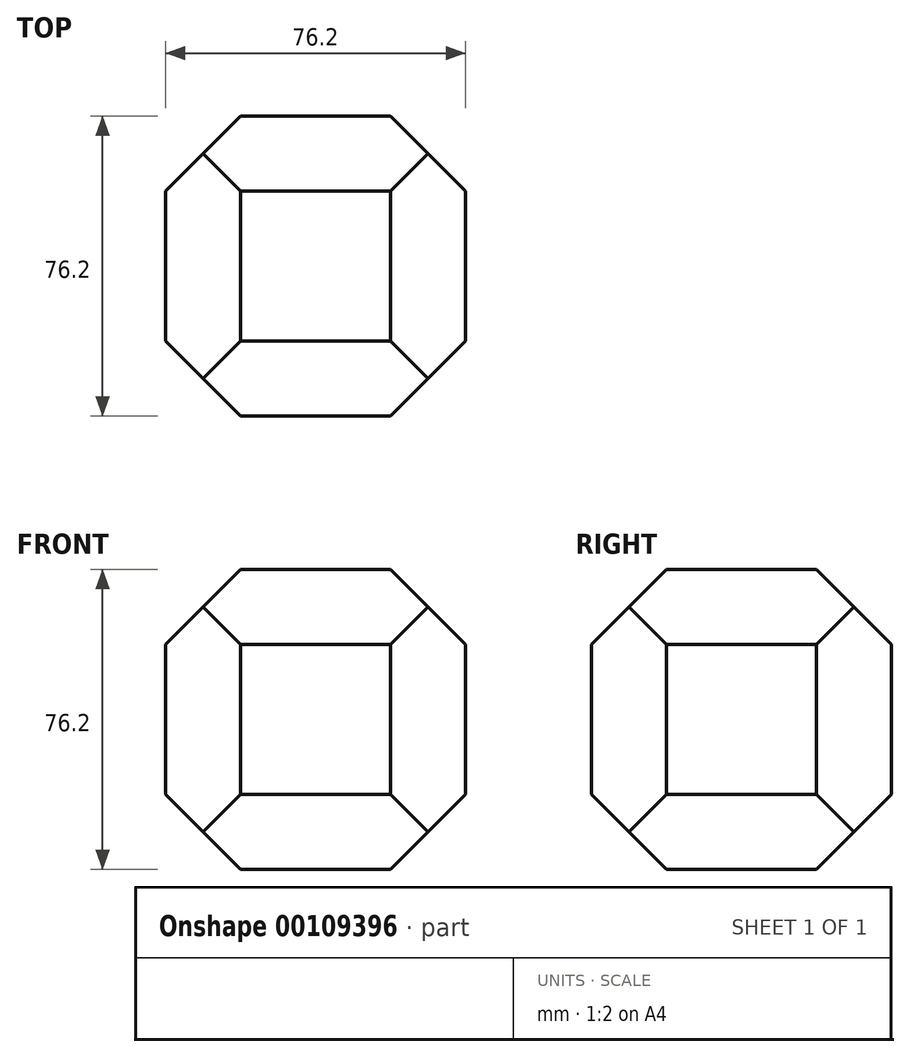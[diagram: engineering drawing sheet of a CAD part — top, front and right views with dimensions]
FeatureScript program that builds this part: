
annotation { "Feature Type Name" : "Feature", "Feature Type Description" : "" }
export const myFeature = defineFeature(function(context is Context, id is Id, definition is map)
    precondition{}
    {
        {
            var Q0;
            Q0=qCreatedBy(makeId("Front.planeOp"),FACE);
            var sketch = newSketch(context, id + "F0", { "sketchPlane" : qUnion([Q0])});
            skLineSegment(sketch, "E0", {"start": v(-38.1, 19.05) * mm, "end": v(-19.05, 38.1) * mm});
            skLineSegment(sketch, "E1", {"start": v(19.05, 38.1) * mm, "end": v(38.1, 19.05) * mm});
            skLineSegment(sketch, "E2", {"start": v(38.1, -19.05) * mm, "end": v(19.05, -38.1) * mm});
            skLineSegment(sketch, "E3", {"start": v(-38.1, -19.05) * mm, "end": v(-19.05, -38.1) * mm});
            skLineSegment(sketch, "E4", {"start": v(-38.1, 19.05) * mm, "end": v(-38.1, -19.05) * mm});
            skLineSegment(sketch, "E5", {"start": v(-19.05, -38.1) * mm, "end": v(19.05, -38.1) * mm});
            skLineSegment(sketch, "E6", {"start": v(38.1, -19.05) * mm, "end": v(38.1, 19.05) * mm});
            skLineSegment(sketch, "E7", {"start": v(19.05, 38.1) * mm, "end": v(-19.05, 38.1) * mm});
            skSolve(sketch);
        }
        {
            var Q0;
            Q0=makeQuery(id+"F0.imprint","IMPRINT",FACE,{"disambiguationData":[TD([[makeQuery(id+"F0.imprint","IMPRINT",EDGE,{"derivedFrom":sQuery(id+"F0.wireOp",EDGE,"E0")}),-1.0]])]});
            extrude(context, id + "F1", {"entities" : qUnion([Q0]), "depth" : 38.1 * mm});
        }
        {
            var Q0;
            Q0 = qSketchRegion(id + "F0", true);
            extrude(context, id + "F2", {"entities" : qUnion([Q0]), "operationType" : NewBodyOperationType.ADD, "oppositeDirection" : true, "depth" : 38.1 * mm});
        }
        {
            var Q0;
            Q0=qCreatedBy(makeId("Right.planeOp"),FACE);
            var sketch = newSketch(context, id + "F3", { "sketchPlane" : qUnion([Q0])});
            skLineSegment(sketch, "E8", {"start": v(-38.1, -19.05) * mm, "end": v(-19.05, -38.1) * mm});
            skLineSegment(sketch, "E9", {"start": v(19.05, -38.1) * mm, "end": v(38.1, -19.05) * mm});
            skLineSegment(sketch, "E10", {"start": v(38.1, 19.05) * mm, "end": v(19.05, 38.1) * mm});
            skLineSegment(sketch, "E11", {"start": v(-38.1, 19.05) * mm, "end": v(-19.05, 38.1) * mm});
            skLineSegment(sketch, "E12", {"start": v(-38.1, 19.05) * mm, "end": v(-38.1, -19.05) * mm});
            skLineSegment(sketch, "E13", {"start": v(-19.05, -38.1) * mm, "end": v(19.05, -38.1) * mm});
            skLineSegment(sketch, "E14", {"start": v(38.1, -19.05) * mm, "end": v(38.1, 19.05) * mm});
            skLineSegment(sketch, "E15", {"start": v(19.05, 38.1) * mm, "end": v(-19.05, 38.1) * mm});
            skLineSegment(sketch, "E16", {"start": v(-38.1, 19.05) * mm, "end": v(-38.1, 38.1) * mm});
            skLineSegment(sketch, "E17", {"start": v(-38.1, 38.1) * mm, "end": v(19.05, 38.1) * mm});
            skLineSegment(sketch, "E18", {"start": v(38.1, 38.1) * mm, "end": v(19.05, 38.1) * mm});
            skLineSegment(sketch, "E19", {"start": v(38.1, 38.1) * mm, "end": v(38.1, 19.05) * mm});
            skLineSegment(sketch, "E20", {"start": v(-38.1, 38.1) * mm, "end": v(-19.05, 38.1) * mm});
            skLineSegment(sketch, "E21", {"start": v(-38.1, 38.1) * mm, "end": v(-38.1, 19.05) * mm});
            skLineSegment(sketch, "E22", {"start": v(-38.1, -19.05) * mm, "end": v(-38.1, -38.1) * mm});
            skLineSegment(sketch, "E23", {"start": v(-38.1, -38.1) * mm, "end": v(-19.05, -38.1) * mm});
            skLineSegment(sketch, "E24", {"start": v(19.05, -38.1) * mm, "end": v(38.1, -38.1) * mm});
            skLineSegment(sketch, "E25", {"start": v(38.1, -38.1) * mm, "end": v(38.1, -19.05) * mm});
            skSolve(sketch);
        }
        {
            var Q0;
            Q0=makeQuery(id+"F3.imprint","IMPRINT",FACE,{"disambiguationData":[TD([[makeQuery(id+"F3.imprint","IMPRINT",EDGE,{"derivedFrom":sQuery(id+"F3.wireOp",EDGE,"E11")}),1.0]])]});
            var Q1;
            Q1=makeQuery(id+"F3.imprint","IMPRINT",FACE,{"disambiguationData":[TD([[makeQuery(id+"F3.imprint","IMPRINT",EDGE,{"derivedFrom":sQuery(id+"F3.wireOp",EDGE,"E10")}),-1.0]])]});
            var Q2;
            Q2=makeQuery(id+"F3.imprint","IMPRINT",FACE,{"disambiguationData":[TD([[makeQuery(id+"F3.imprint","IMPRINT",EDGE,{"derivedFrom":sQuery(id+"F3.wireOp",EDGE,"E9")}),-1.0]])]});
            var Q3;
            Q3=makeQuery(id+"F3.imprint","IMPRINT",FACE,{"disambiguationData":[TD([[makeQuery(id+"F3.imprint","IMPRINT",EDGE,{"derivedFrom":sQuery(id+"F3.wireOp",EDGE,"E8")}),-1.0]])]});
            extrude(context, id + "F4", {"entities" : qUnion([Q0, Q1, Q2, Q3]), "operationType" : NewBodyOperationType.REMOVE, "oppositeDirection" : true, "depth" : 38.1 * mm});
        }
        {
            var Q0;
            Q0=makeQuery(id+"F3.imprint","IMPRINT",FACE,{"disambiguationData":[TD([[makeQuery(id+"F3.imprint","IMPRINT",EDGE,{"derivedFrom":sQuery(id+"F3.wireOp",EDGE,"E11")}),1.0]])]});
            var Q1;
            Q1=makeQuery(id+"F3.imprint","IMPRINT",FACE,{"disambiguationData":[TD([[makeQuery(id+"F3.imprint","IMPRINT",EDGE,{"derivedFrom":sQuery(id+"F3.wireOp",EDGE,"E10")}),-1.0]])]});
            var Q2;
            Q2=makeQuery(id+"F3.imprint","IMPRINT",FACE,{"disambiguationData":[TD([[makeQuery(id+"F3.imprint","IMPRINT",EDGE,{"derivedFrom":sQuery(id+"F3.wireOp",EDGE,"E9")}),-1.0]])]});
            var Q3;
            Q3=makeQuery(id+"F3.imprint","IMPRINT",FACE,{"disambiguationData":[TD([[makeQuery(id+"F3.imprint","IMPRINT",EDGE,{"derivedFrom":sQuery(id+"F3.wireOp",EDGE,"E8")}),-1.0]])]});
            extrude(context, id + "F5", {"entities" : qUnion([Q0, Q1, Q2, Q3]), "operationType" : NewBodyOperationType.REMOVE, "depth" : 38.1 * mm});
        }
        {
            var Q0;
            Q0=qCreatedBy(makeId("Top.planeOp"),FACE);
            var sketch = newSketch(context, id + "F6", { "sketchPlane" : qUnion([Q0])});
            skLineSegment(sketch, "E26", {"start": v(19.05, -38.1) * mm, "end": v(38.1, -19.05) * mm});
            skLineSegment(sketch, "E27", {"start": v(38.1, 19.05) * mm, "end": v(19.05, 38.1) * mm});
            skLineSegment(sketch, "E28", {"start": v(-19.05, 38.1) * mm, "end": v(-38.1, 19.05) * mm});
            skLineSegment(sketch, "E29", {"start": v(-19.05, -38.1) * mm, "end": v(-38.1, -19.05) * mm});
            skLineSegment(sketch, "E30", {"start": v(-19.05, -38.1) * mm, "end": v(19.05, -38.1) * mm});
            skLineSegment(sketch, "E31", {"start": v(38.1, -19.05) * mm, "end": v(38.1, 19.05) * mm});
            skLineSegment(sketch, "E32", {"start": v(19.05, 38.1) * mm, "end": v(-19.05, 38.1) * mm});
            skLineSegment(sketch, "E33", {"start": v(-38.1, 19.05) * mm, "end": v(-38.1, -19.05) * mm});
            skLineSegment(sketch, "E34", {"start": v(-38.1, -19.05) * mm, "end": v(-38.1, -38.1) * mm});
            skLineSegment(sketch, "E35", {"start": v(-38.1, -38.1) * mm, "end": v(-19.05, -38.1) * mm});
            skLineSegment(sketch, "E36", {"start": v(-38.1, 19.05) * mm, "end": v(-38.1, 38.1) * mm});
            skLineSegment(sketch, "E37", {"start": v(-38.1, 38.1) * mm, "end": v(-19.05, 38.1) * mm});
            skLineSegment(sketch, "E38", {"start": v(19.05, 38.1) * mm, "end": v(38.1, 38.1) * mm});
            skLineSegment(sketch, "E39", {"start": v(38.1, 38.1) * mm, "end": v(38.1, 19.05) * mm});
            skLineSegment(sketch, "E40", {"start": v(19.05, -38.1) * mm, "end": v(38.1, -38.1) * mm});
            skLineSegment(sketch, "E41", {"start": v(38.1, -38.1) * mm, "end": v(38.1, -19.05) * mm});
            skSolve(sketch);
        }
        {
            var Q0;
            Q0=makeQuery(id+"F6.imprint","IMPRINT",FACE,{"disambiguationData":[TD([[makeQuery(id+"F6.imprint","IMPRINT",EDGE,{"derivedFrom":sQuery(id+"F6.wireOp",EDGE,"E26")}),-1.0]])]});
            var Q1;
            Q1=makeQuery(id+"F6.imprint","IMPRINT",FACE,{"disambiguationData":[TD([[makeQuery(id+"F6.imprint","IMPRINT",EDGE,{"derivedFrom":sQuery(id+"F6.wireOp",EDGE,"E27")}),-1.0]])]});
            var Q2;
            Q2=makeQuery(id+"F6.imprint","IMPRINT",FACE,{"disambiguationData":[TD([[makeQuery(id+"F6.imprint","IMPRINT",EDGE,{"derivedFrom":sQuery(id+"F6.wireOp",EDGE,"E28")}),-1.0]])]});
            var Q3;
            Q3=makeQuery(id+"F6.imprint","IMPRINT",FACE,{"disambiguationData":[TD([[makeQuery(id+"F6.imprint","IMPRINT",EDGE,{"derivedFrom":sQuery(id+"F6.wireOp",EDGE,"E29")}),1.0]])]});
            extrude(context, id + "F7", {"entities" : qUnion([Q0, Q1, Q2, Q3]), "operationType" : NewBodyOperationType.REMOVE, "oppositeDirection" : true, "depth" : 38.1 * mm});
        }
        {
            var Q0;
            Q0=makeQuery(id+"F6.imprint","IMPRINT",FACE,{"disambiguationData":[TD([[makeQuery(id+"F6.imprint","IMPRINT",EDGE,{"derivedFrom":sQuery(id+"F6.wireOp",EDGE,"E26")}),-1.0]])]});
            var Q1;
            Q1=makeQuery(id+"F6.imprint","IMPRINT",FACE,{"disambiguationData":[TD([[makeQuery(id+"F6.imprint","IMPRINT",EDGE,{"derivedFrom":sQuery(id+"F6.wireOp",EDGE,"E29")}),1.0]])]});
            var Q2;
            Q2=makeQuery(id+"F6.imprint","IMPRINT",FACE,{"disambiguationData":[TD([[makeQuery(id+"F6.imprint","IMPRINT",EDGE,{"derivedFrom":sQuery(id+"F6.wireOp",EDGE,"E28")}),-1.0]])]});
            var Q3;
            Q3=makeQuery(id+"F6.imprint","IMPRINT",FACE,{"disambiguationData":[TD([[makeQuery(id+"F6.imprint","IMPRINT",EDGE,{"derivedFrom":sQuery(id+"F6.wireOp",EDGE,"E27")}),-1.0]])]});
            extrude(context, id + "F8", {"entities" : qUnion([Q0, Q1, Q2, Q3]), "operationType" : NewBodyOperationType.REMOVE, "depth" : 38.1 * mm});
        }
    });
